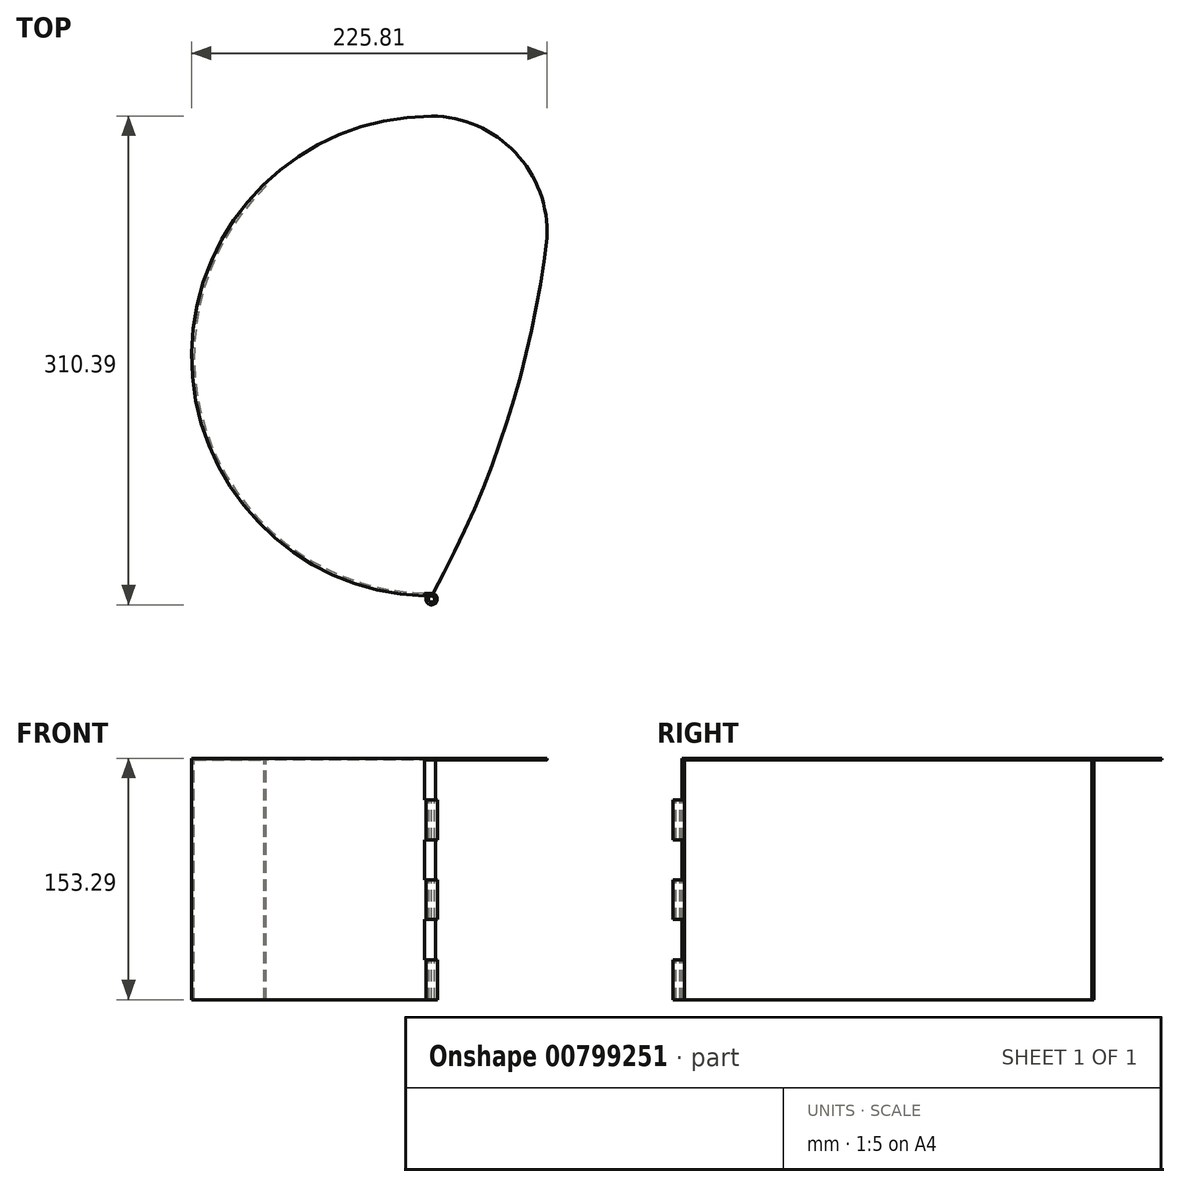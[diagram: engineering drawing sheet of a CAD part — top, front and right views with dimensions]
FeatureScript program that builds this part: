
annotation { "Feature Type Name" : "Feature", "Feature Type Description" : "" }
export const myFeature = defineFeature(function(context is Context, id is Id, definition is map)
    precondition{}
    {
        {
            var Q0;
            Q0=qCreatedBy(makeId("Top.planeOp"),FACE);
            var sketch = newSketch(context, id + "F0", { "sketchPlane" : qUnion([Q0])});
            skArc(sketch, "E0", {"start": v(0, 152.4) * mm, "mid": v(-152.4, 0) * mm, "end": v(0, -152.4) * mm});
            skArc(sketch, "E1.MirrorCS", {"start": v(0, 152.4) * mm, "mid": v(53.18, 129.3) * mm, "end": v(73.32, 74.93) * mm});
            skArc(sketch, "E2.MirrorCS", {"start": v(73.32, 74.93) * mm, "mid": v(47.74, -42.31) * mm, "end": v(0, -152.4) * mm});
            skPoint(sketch, "E3.start.orphan", {"position": v(0, 152.4) * mm});
            skPoint(sketch, "E4.end.orphan", {"position": v(0, -152.4) * mm});
            skPoint(sketch, "E4.start.orphan", {"position": v(-73.32, 74.93) * mm});
            skSolve(sketch);
        }
        {
            var Q0;
            Q0=makeQuery(id+"F0.imprint","IMPRINT",FACE,{"disambiguationData":[TD([[makeQuery(id+"F0.imprint","IMPRINT",EDGE,{"derivedFrom":sQuery(id+"F0.wireOp",EDGE,"E0")}),1.0]])]});
            extrude(context, id + "F1", {"entities" : qUnion([Q0]), "depth" : 0.89 * mm, "offsetDistance" : 25.4 * mm});
        }
        {
            var Q0;
            Q0=makeQuery(id+"F1.opExtrude","CAP_FACE",FACE,{"disambiguationData":[OSD([sQuery(id+"F0.wireOp",EDGE,"E0"),sQuery(id+"F0.wireOp",EDGE,"E1.MirrorCS"),sQuery(id+"F0.wireOp",EDGE,"E2.MirrorCS")])],"isStart":true});
            var sketch = newSketch(context, id + "F2", { "sketchPlane" : qUnion([Q0])});
            skArc(sketch, "E5", {"start": v(0, 152.4) * mm, "mid": v(-141.61, 57.58) * mm, "end": v(-106.35, -109.16) * mm});
            skLineSegment(sketch, "E6", {"start": v(-106.35, -109.16) * mm, "end": v(-105.18, -107.97) * mm});
            skArc(sketch, "E7", {"start": v(0, 150.74) * mm, "mid": v(-139.64, 56.77) * mm, "end": v(-105.18, -107.97) * mm});
            skArc(sketch, "E8", {"start": v(0, 152.46) * mm, "mid": v(1.01, 155.98) * mm, "end": v(-1.72, 153.53) * mm});
            skLineSegment(sketch, "E9", {"start": v(-1.72, 153.53) * mm, "end": v(-3.26, 152.78) * mm});
            skArc(sketch, "E10", {"start": v(0, 150.74) * mm, "mid": v(1.93, 157.43) * mm, "end": v(-3.26, 152.78) * mm});
            skLineSegment(sketch, "E11", {"start": v(0, 152.4) * mm, "end": v(0, 152.46) * mm});
            skSolve(sketch);
        }
        {
            var Q0;
            Q0=makeQuery(id+"F2.imprint","IMPRINT",FACE,{"disambiguationData":[TD([[makeQuery(id+"F2.imprint","IMPRINT",EDGE,{"derivedFrom":sQuery(id+"F2.wireOp",EDGE,"E8")}),-1.0]])]});
            var Q1;
            {var subQ4=sQuery(id+"F2.wireOp",EDGE,"E6");Q1=makeQuery(id+"F2.imprint","IMPRINT",FACE,{"disambiguationData":[TD([[makeQuery(id+"F2.imprint","IMPRINT",EDGE,{"derivedFrom":subQ4}),1.0]])]});}
            extrude(context, id + "F3", {"entities" : qUnion([Q0, Q1]), "operationType" : NewBodyOperationType.ADD, "depth" : 152.4 * mm, "offsetDistance" : 25.4 * mm});
        }
        {
            var Q0;
            Q0=qCreatedBy(makeId("Right.planeOp"),FACE);
            var sketch = newSketch(context, id + "F4", { "sketchPlane" : qUnion([Q0])});
            skLineSegment(sketch, "E12", {"start": v(-150.75, 0) * mm, "end": v(-150.75, 1.18) * mm});
            skLineSegment(sketch, "E13", {"start": v(-150.75, 1.18) * mm, "end": v(-161.25, 1.18) * mm});
            skLineSegment(sketch, "E14", {"start": v(-161.25, 1.18) * mm, "end": v(-161.25, 0) * mm});
            skLineSegment(sketch, "E15", {"start": v(-151.66, 0) * mm, "end": v(-151.66, -25.39) * mm});
            skLineSegment(sketch, "E16", {"start": v(-151.66, -25.39) * mm, "end": v(-161.25, -25.39) * mm});
            skLineSegment(sketch, "E17", {"start": v(-161.25, -25.39) * mm, "end": v(-161.25, -50.78) * mm});
            skLineSegment(sketch, "E18", {"start": v(-161.25, -50.78) * mm, "end": v(-151.66, -50.78) * mm});
            skLineSegment(sketch, "E19", {"start": v(-151.66, -50.78) * mm, "end": v(-151.66, -76.17) * mm});
            skLineSegment(sketch, "E20", {"start": v(-151.66, -76.17) * mm, "end": v(-161.25, -76.17) * mm});
            skLineSegment(sketch, "E21", {"start": v(-161.25, -76.17) * mm, "end": v(-161.25, -101.56) * mm});
            skLineSegment(sketch, "E22", {"start": v(-161.25, -101.56) * mm, "end": v(-151.66, -101.56) * mm});
            skLineSegment(sketch, "E23", {"start": v(-151.66, -101.56) * mm, "end": v(-151.66, -126.97) * mm});
            skLineSegment(sketch, "E24", {"start": v(-151.66, -126.97) * mm, "end": v(-161.25, -126.97) * mm});
            skLineSegment(sketch, "E25", {"start": v(-161.25, -126.97) * mm, "end": v(-161.25, -152.88) * mm});
            skLineSegment(sketch, "E26", {"start": v(-161.25, -152.88) * mm, "end": v(-165.63, -152.88) * mm});
            skLineSegment(sketch, "E27", {"start": v(-165.63, -152.88) * mm, "end": v(-165.63, 0) * mm});
            skLineSegment(sketch, "E28", {"start": v(-165.63, 0) * mm, "end": v(-161.25, 0) * mm});
            skLineSegment(sketch, "E29", {"start": v(-151.66, 0) * mm, "end": v(-150.75, 0) * mm});
            skSolve(sketch);
        }
        {
            var Q0;
            Q0=makeQuery(id+"F4.imprint","IMPRINT",FACE,{"disambiguationData":[TD([[makeQuery(id+"F4.imprint","IMPRINT",EDGE,{"derivedFrom":sQuery(id+"F4.wireOp",EDGE,"E12")}),1.0]])]});
            extrude(context, id + "F5", {"entities" : qUnion([Q0]), "operationType" : NewBodyOperationType.REMOVE, "endBound" : BoundingType.SYMMETRIC, "oppositeDirection" : true, "depth" : 8.64 * mm, "offsetDistance" : 25.4 * mm});
        }
    });
